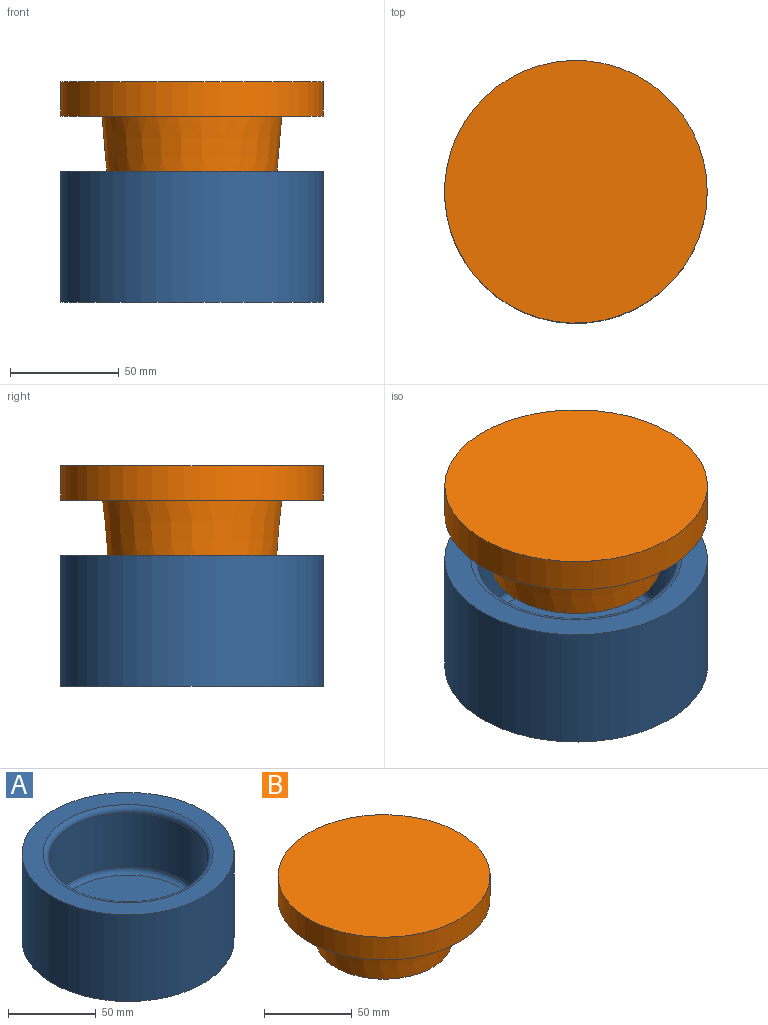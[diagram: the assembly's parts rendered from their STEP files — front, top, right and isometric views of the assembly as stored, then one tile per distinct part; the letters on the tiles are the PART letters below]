
ASSEMBLY  parts=2 mates=1
PART A: 7 faces, bbox 120.7x120.7x60.3 mm
  f0: cylinder r=45.09mm len=90.17mm, axis (0,0,1), area 10714.5mm2, adj f1,f6
  f1: torus R=48.4mm, axis (0,0,1), area 1513.7mm2, adj f0,f2
  f2: plane 120.65x120.65mm, normal (0,0,1), area 4073.7mm2, adj f1,f3
  f3: cylinder r=60.32mm len=120.65mm, axis (0,0,1), area 22865.2mm2, adj f2,f4
  f4: plane 120.65x120.65mm, normal (0,0,-1), area 11432.6mm2, adj f3
  f5: plane 83.54x83.54mm, normal (0,0,1), area 5481.7mm2, adj f6
  f6: torus R=41.77mm, axis (0,0,1), area 1435mm2, adj f0,f5
PART B: 9 faces, bbox 121.1x121.1x44.5 mm
  f0: torus R=47.92mm, axis (0,0,1), area 1551.6mm2, adj f1,f8
  f1: plane 95.84x95.84mm, normal (0,0,-1), area 1862.4mm2, adj f0,f2
  f2: cone r=41.27mm half-angle=5deg, axis (0,0,1), area 7218.2mm2, adj f1,f3
  f3: plane 77.55x77.55mm, normal (0,0,-1), area 4723mm2, adj f2
  f4: plane 120.65x120.65mm, normal (0,0,1), area 11432.6mm2, adj f5
  f5: cylinder r=60.32mm len=120.65mm, axis (0,0,1), area 6017.2mm2, adj f4,f6
  f6: plane 120.65x120.65mm, normal (0,0,-1), area 2179.4mm2, adj f5,f7
  f7: torus R=54.27mm, axis (0,0,1), area 1832.6mm2, adj f6,f8
  f8: plane 108.54x108.54mm, normal (0,0,-1), area 2038.7mm2, adj f0,f7
PLACE A t=(-12.65,4.44,47.44)mm
PLACE B t=(-12.65,4.44,10.92)mm
MATE pin_slot B.f0 <-> A.f0  axis (0,0,1) through (-12.65,4.44,24.48)mm
